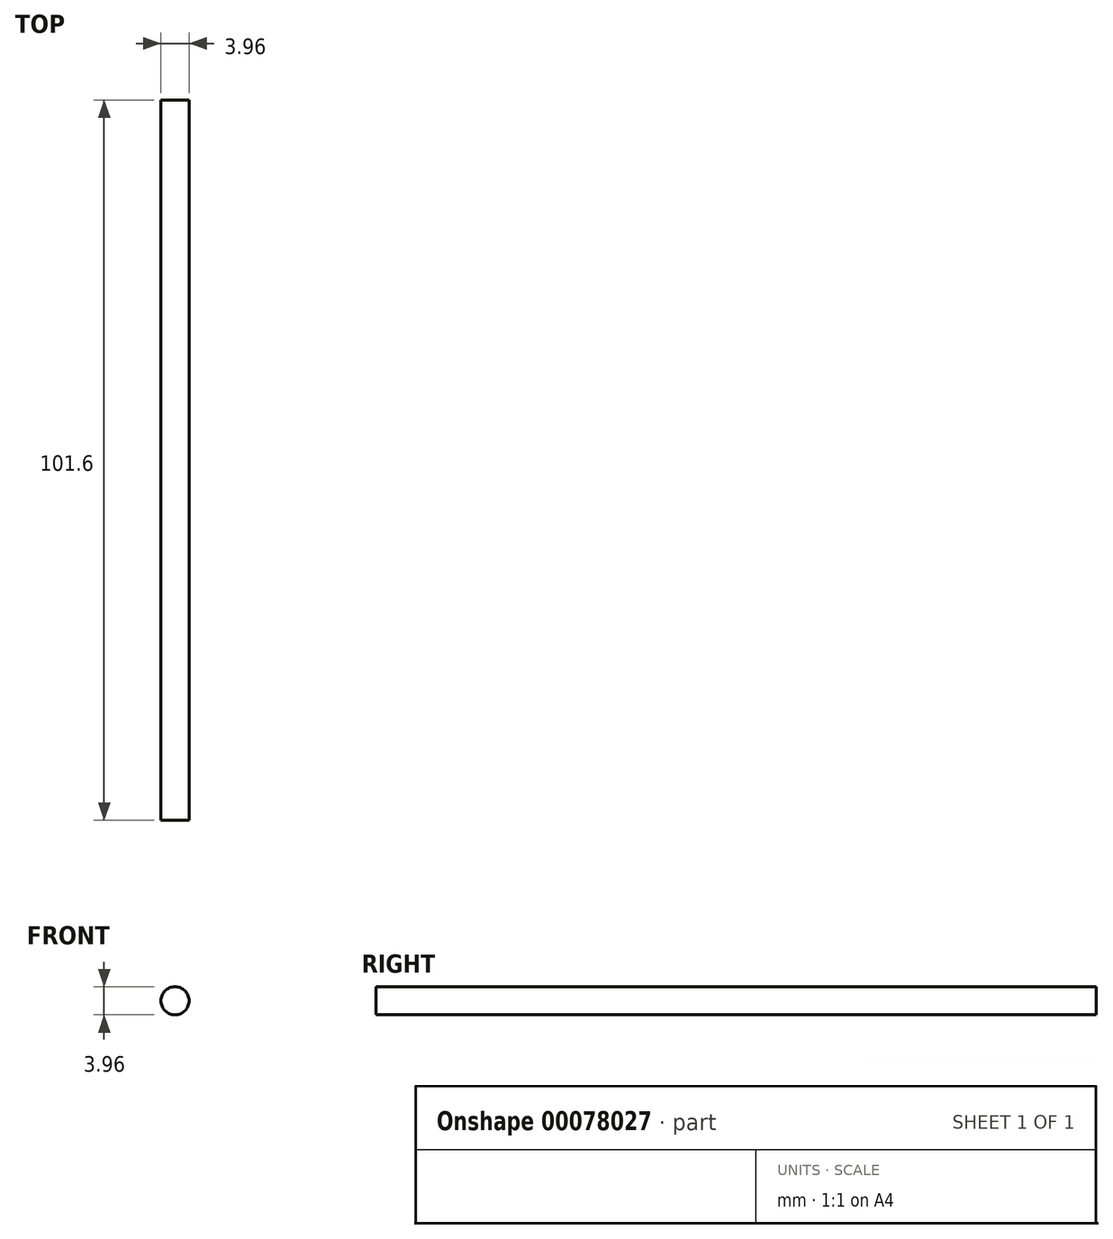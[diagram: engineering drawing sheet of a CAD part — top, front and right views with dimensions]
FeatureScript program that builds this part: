
annotation { "Feature Type Name" : "Feature", "Feature Type Description" : "" }
export const myFeature = defineFeature(function(context is Context, id is Id, definition is map)
    precondition{}
    {
        {
            var Q0;
            Q0=qCreatedBy(makeId("Front.planeOp"),FACE);
            var sketch = newSketch(context, id + "F0", { "sketchPlane" : qUnion([Q0])});
            skCircle(sketch, "E0", {"center": v(0, 0) * mm, "radius": 1.98 * mm});
            skSolve(sketch);
        }
        {
            var Q0;
            Q0 = qSketchRegion(id + "F0", true);
            extrude(context, id + "F1", {"entities" : qUnion([Q0]), "endBound" : BoundingType.SYMMETRIC, "depth" : 101.6 * mm});
        }
    });
